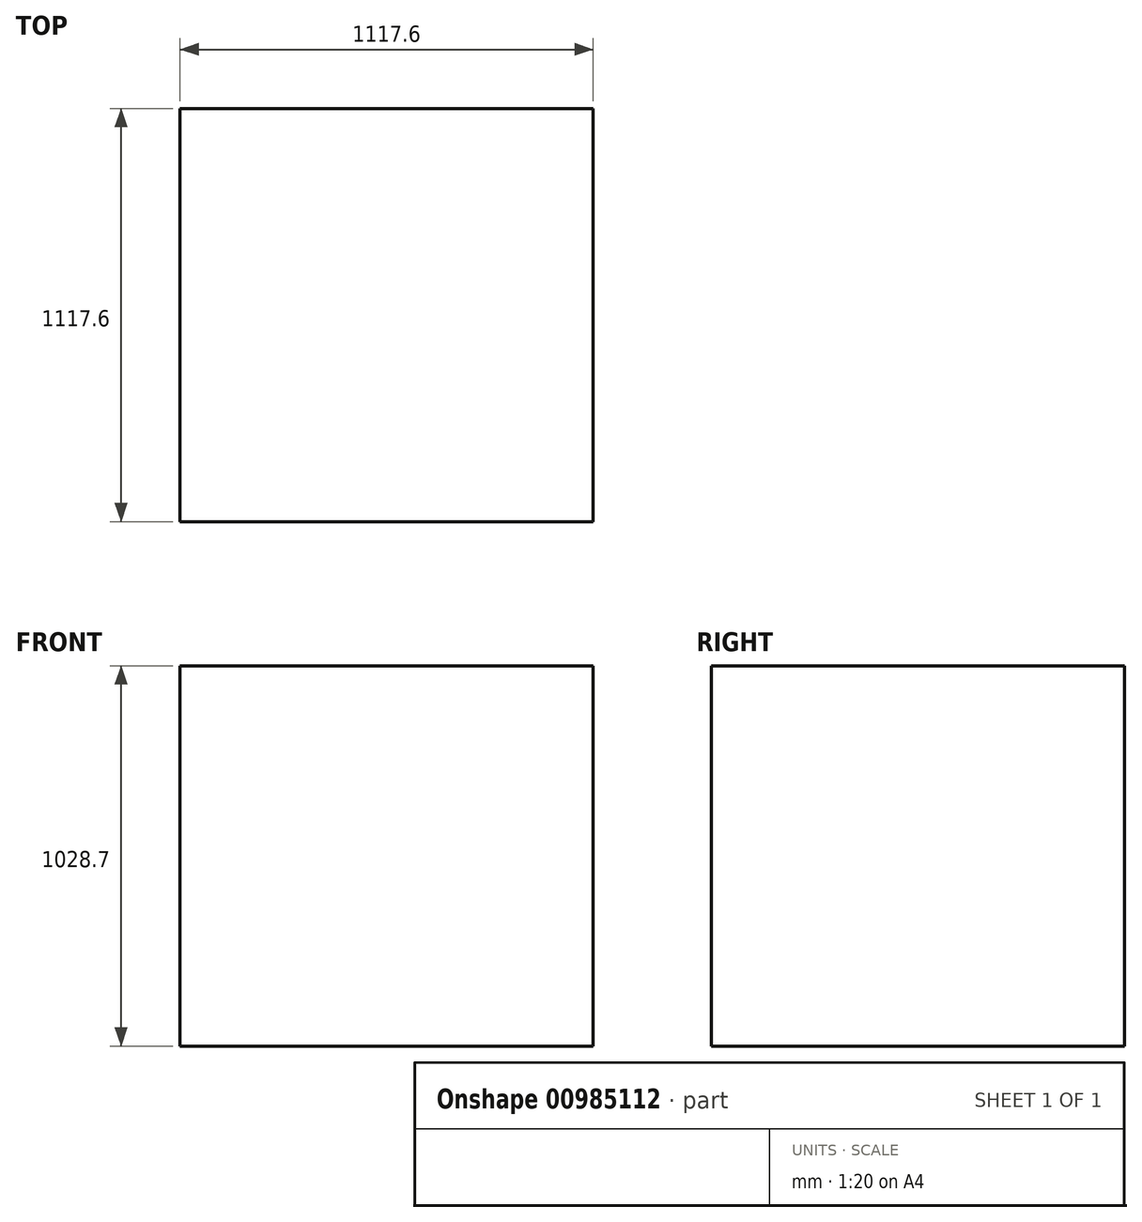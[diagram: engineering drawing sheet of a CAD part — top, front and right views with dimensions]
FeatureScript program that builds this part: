
annotation { "Feature Type Name" : "Feature", "Feature Type Description" : "" }
export const myFeature = defineFeature(function(context is Context, id is Id, definition is map)
    precondition{}
    {
        {
            var Q0;
            Q0=qCreatedBy(makeId("Top.planeOp"),FACE);
            var sketch = newSketch(context, id + "F0", { "sketchPlane" : qUnion([Q0])});
            skLineSegment(sketch, "E0.bottom", {"start": v(558.8, -558.8) * mm, "end": v(-558.8, -558.8) * mm});
            skLineSegment(sketch, "E0.top", {"start": v(558.8, 558.8) * mm, "end": v(-558.8, 558.8) * mm});
            skLineSegment(sketch, "E0.left", {"start": v(558.8, -558.8) * mm, "end": v(558.8, 558.8) * mm});
            skLineSegment(sketch, "E0.right", {"start": v(-558.8, -558.8) * mm, "end": v(-558.8, 558.8) * mm});
            skPoint(sketch, "E0.middle", {"position": v(0, 0) * mm});
            skSolve(sketch);
        }
        {
            var Q0;
            Q0 = qSketchRegion(id + "F0", true);
            extrude(context, id + "F1", {"entities" : qUnion([Q0]), "depth" : 1028.7 * mm, "offsetDistance" : 25.4 * mm});
        }
    });
